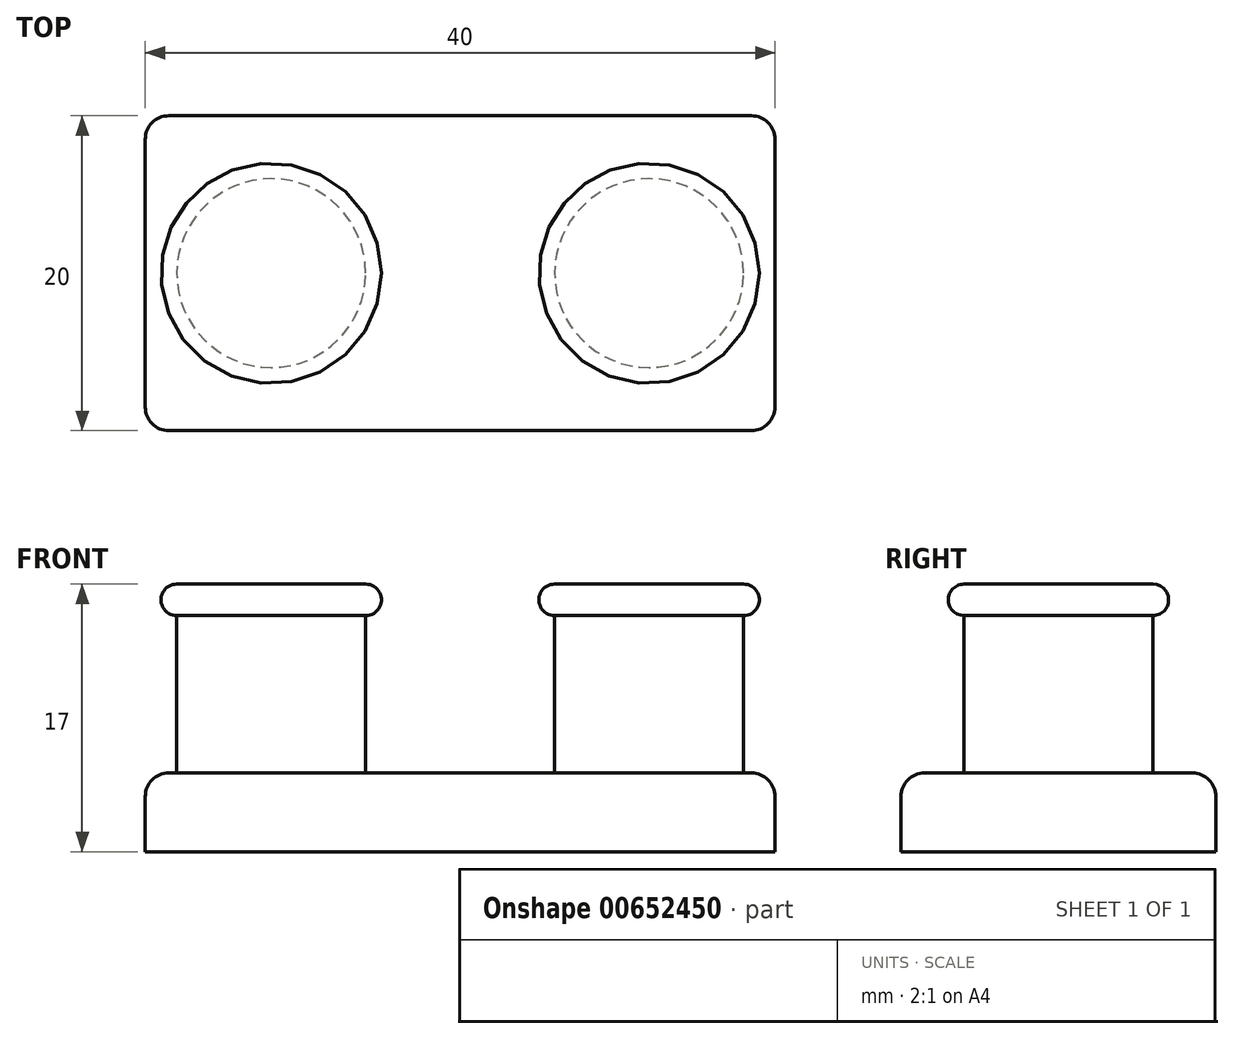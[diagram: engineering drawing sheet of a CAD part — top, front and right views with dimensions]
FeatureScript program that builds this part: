
annotation { "Feature Type Name" : "Feature", "Feature Type Description" : "" }
export const myFeature = defineFeature(function(context is Context, id is Id, definition is map)
    precondition{}
    {
        {
            var Q0;
            Q0=qCreatedBy(makeId("Top.planeOp"),FACE);
            var sketch = newSketch(context, id + "F0", { "sketchPlane" : qUnion([Q0])});
            skLineSegment(sketch, "E0.bottom", {"start": v(20, -10) * mm, "end": v(-20, -10) * mm});
            skLineSegment(sketch, "E0.top", {"start": v(20, 10) * mm, "end": v(-20, 10) * mm});
            skLineSegment(sketch, "E0.left", {"start": v(20, -10) * mm, "end": v(20, 10) * mm});
            skLineSegment(sketch, "E0.right", {"start": v(-20, -10) * mm, "end": v(-20, 10) * mm});
            skPoint(sketch, "E0.middle", {"position": v(0, 0) * mm});
            skSolve(sketch);
        }
        {
            var Q0;
            Q0 = qSketchRegion(id + "F0", true);
            extrude(context, id + "F1", {"entities" : qUnion([Q0]), "depth" : 5 * mm, "offsetDistance" : 25 * mm});
        }
        {
            var Q0;
            Q0=makeQuery(id+"F1.opExtrude","CAP_FACE",FACE,{"disambiguationData":[OSD([sQuery(id+"F0.wireOp",EDGE,"E0.bottom"),sQuery(id+"F0.wireOp",EDGE,"E0.top"),sQuery(id+"F0.wireOp",EDGE,"E0.left"),sQuery(id+"F0.wireOp",EDGE,"E0.right")])],"isStart":false});
            var sketch = newSketch(context, id + "F2", { "sketchPlane" : qUnion([Q0])});
            skCircle(sketch, "E1", {"center": v(-12, 0) * mm, "radius": 6 * mm});
            skCircle(sketch, "E2", {"center": v(12, 0) * mm, "radius": 6 * mm});
            skSolve(sketch);
        }
        {
            var Q0;
            Q0 = qSketchRegion(id + "F2", true);
            extrude(context, id + "F3", {"entities" : qUnion([Q0]), "operationType" : NewBodyOperationType.ADD, "depth" : 10 * mm, "offsetDistance" : 25 * mm});
        }
        {
            var Q0;
            Q0=makeQuery(id+"F3.opExtrude","CAP_FACE",FACE,{"disambiguationData":[OSD([sQuery(id+"F2.wireOp",EDGE,"E1")])],"isStart":false});
            var sketch = newSketch(context, id + "F4", { "sketchPlane" : qUnion([Q0])});
            skCircle(sketch, "E3", {"center": v(-12, 0) * mm, "radius": 7 * mm});
            skSolve(sketch);
        }
        {
            var Q0;
            Q0 = qSketchRegion(id + "F4", true);
            extrude(context, id + "F5", {"entities" : qUnion([Q0]), "operationType" : NewBodyOperationType.ADD, "depth" : 2 * mm, "offsetDistance" : 25 * mm});
        }
        {
            var Q0;
            Q0=makeQuery(id+"F3.opExtrude","CAP_FACE",FACE,{"disambiguationData":[OSD([sQuery(id+"F2.wireOp",EDGE,"E2")])],"isStart":false});
            var sketch = newSketch(context, id + "F6", { "sketchPlane" : qUnion([Q0])});
            skCircle(sketch, "E4", {"center": v(12, 0) * mm, "radius": 7 * mm});
            skSolve(sketch);
        }
        {
            var Q0;
            Q0 = qSketchRegion(id + "F6", true);
            extrude(context, id + "F7", {"entities" : qUnion([Q0]), "operationType" : NewBodyOperationType.ADD, "depth" : 2 * mm, "offsetDistance" : 25 * mm});
        }
        {
            var Q0;
            Q0=makeQuery(id+"F1.opExtrude","CAP_EDGE",EDGE,{"disambiguationData":[OSD([sQuery(id+"F0.wireOp",EDGE,"E0.bottom")])],"isStart":false});
            var Q1;
            Q1=makeQuery(id+"F1.opExtrude","CAP_EDGE",EDGE,{"disambiguationData":[OSD([sQuery(id+"F0.wireOp",EDGE,"E0.right")])],"isStart":false});
            var Q2;
            Q2=makeQuery(id+"F1.opExtrude","CAP_EDGE",EDGE,{"disambiguationData":[OSD([sQuery(id+"F0.wireOp",EDGE,"E0.top")])],"isStart":false});
            var Q3;
            Q3=makeQuery(id+"F1.opExtrude","CAP_EDGE",EDGE,{"disambiguationData":[OSD([sQuery(id+"F0.wireOp",EDGE,"E0.left")])],"isStart":false});
            var Q4;
            Q4=makeQuery(id+"F1.opExtrude","SWEPT_EDGE",EDGE,{"disambiguationData":[OSD([sQuery(id+"F0.wireOp",EDGE,"E0.bottom"),sQuery(id+"F0.wireOp",EDGE,"E0.left")])]});
            var Q5;
            Q5=makeQuery(id+"F1.opExtrude","SWEPT_EDGE",EDGE,{"disambiguationData":[OSD([sQuery(id+"F0.wireOp",EDGE,"E0.top"),sQuery(id+"F0.wireOp",EDGE,"E0.left")])]});
            var Q6;
            Q6=makeQuery(id+"F1.opExtrude","SWEPT_EDGE",EDGE,{"disambiguationData":[OSD([sQuery(id+"F0.wireOp",EDGE,"E0.top"),sQuery(id+"F0.wireOp",EDGE,"E0.right")])]});
            var Q7;
            Q7=makeQuery(id+"F1.opExtrude","SWEPT_EDGE",EDGE,{"disambiguationData":[OSD([sQuery(id+"F0.wireOp",EDGE,"E0.bottom"),sQuery(id+"F0.wireOp",EDGE,"E0.right")])]});
            fillet(context, id + "F8", {"entities" : qUnion([Q0, Q1, Q2, Q3, Q4, Q5, Q6, Q7]), "radius" : 1.5 * mm, "tangentPropagation" : true, "allowEdgeOverflow" : false});
        }
        {
            var Q0;
            Q0=makeQuery(id+"F5.opExtrude","CAP_EDGE",EDGE,{"disambiguationData":[OSD([sQuery(id+"F4.wireOp",EDGE,"E3")])],"isStart":true});
            var Q1;
            Q1=makeQuery(id+"F7.opExtrude","CAP_EDGE",EDGE,{"disambiguationData":[OSD([sQuery(id+"F6.wireOp",EDGE,"E4")])],"isStart":true});
            var Q2;
            Q2=makeQuery(id+"F5.opExtrude","CAP_EDGE",EDGE,{"disambiguationData":[OSD([sQuery(id+"F4.wireOp",EDGE,"E3")])],"isStart":false});
            var Q3;
            Q3=makeQuery(id+"F7.opExtrude","CAP_EDGE",EDGE,{"disambiguationData":[OSD([sQuery(id+"F6.wireOp",EDGE,"E4")])],"isStart":false});
            fillet(context, id + "F9", {"entities" : qUnion([Q0, Q1, Q2, Q3]), "radius" : 1 * mm, "tangentPropagation" : true, "allowEdgeOverflow" : false});
        }
    });
